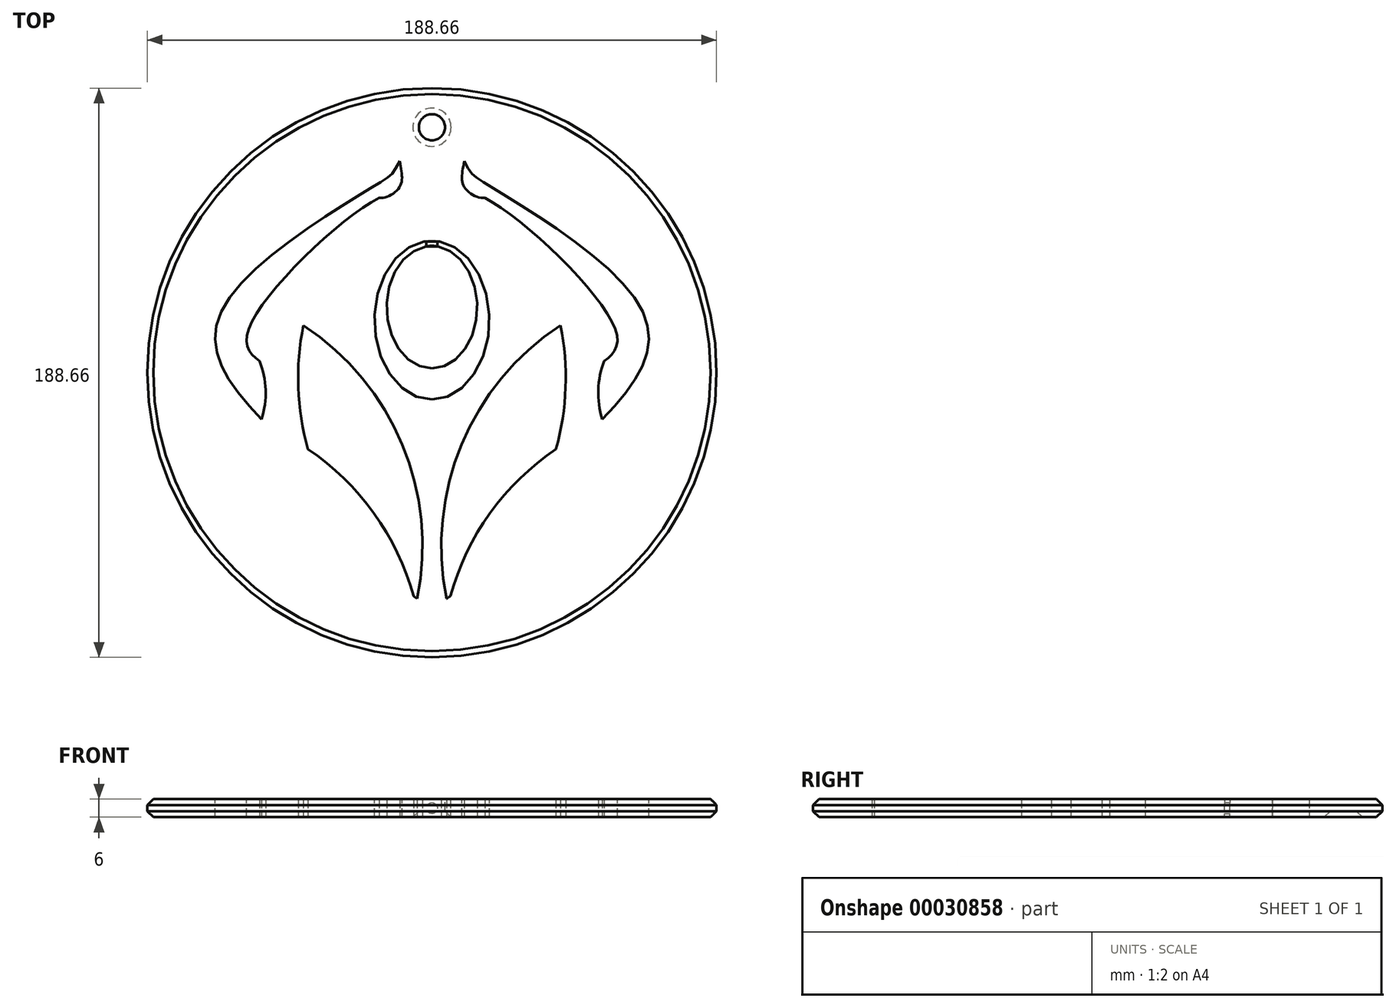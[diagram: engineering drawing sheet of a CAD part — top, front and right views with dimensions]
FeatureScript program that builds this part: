
annotation { "Feature Type Name" : "Feature", "Feature Type Description" : "" }
export const myFeature = defineFeature(function(context is Context, id is Id, definition is map)
    precondition{}
    {
        {
            var Q0;
            Q0=qCreatedBy(makeId("Top.planeOp"),FACE);
            var sketch = newSketch(context, id + "F0", { "sketchPlane" : qUnion([Q0])});
            skLineSegment(sketch, "E0", {"start": v(-75.5, -12.71) * mm, "end": v(-9.56, -74.3) * mm, "construction": true});
            skLineSegment(sketch, "E1", {"start": v(-4.86, -71.61) * mm, "end": v(-42.6, 18.94) * mm, "construction": true});
            skArc(sketch, "E2", {"start": v(-75.5, -12.71) * mm, "mid": v(-51.74, -53.37) * mm, "end": v(-9.56, -74.3) * mm});
            skArc(sketch, "E3", {"start": v(-4.86, -71.61) * mm, "mid": v(-9.83, -20.55) * mm, "end": v(-42.6, 18.94) * mm});
            skArc(sketch, "E4.MirrorCS", {"start": v(-75.5, -12.71) * mm, "mid": v(-33.32, -33.65) * mm, "end": v(-9.56, -74.3) * mm});
            skArc(sketch, "E5.0", {"start": v(-41.12, -22.06) * mm, "mid": v(-19.25, -43.28) * mm, "end": v(-6.12, -70.78) * mm});
            skArc(sketch, "E6.MirrorCS", {"start": v(-4.86, -71.61) * mm, "mid": v(-5.5, -71.2) * mm, "end": v(-6.12, -70.78) * mm});
            skArc(sketch, "E7.trimOffspring", {"start": v(-41.12, -22.06) * mm, "mid": v(-44.3, -1.65) * mm, "end": v(-42.6, 18.94) * mm});
            skArc(sketch, "E8.MirrorCS", {"start": v(75.5, -12.71) * mm, "mid": v(51.74, -53.37) * mm, "end": v(9.56, -74.3) * mm});
            skArc(sketch, "E9.MirrorCS", {"start": v(75.5, -12.71) * mm, "mid": v(33.32, -33.65) * mm, "end": v(9.56, -74.3) * mm});
            skArc(sketch, "E10.MirrorCS", {"start": v(41.12, -22.06) * mm, "mid": v(44.3, -1.65) * mm, "end": v(42.6, 18.94) * mm});
            skArc(sketch, "E11.MirrorCS", {"start": v(41.12, -22.06) * mm, "mid": v(19.25, -43.28) * mm, "end": v(6.12, -70.78) * mm});
            skArc(sketch, "E12.MirrorCS", {"start": v(4.86, -71.61) * mm, "mid": v(9.83, -20.55) * mm, "end": v(42.6, 18.94) * mm});
            skArc(sketch, "E13.MirrorCS", {"start": v(4.86, -71.61) * mm, "mid": v(5.5, -71.2) * mm, "end": v(6.12, -70.78) * mm});
            skSolve(sketch);
        }
        {
            var Q0;
            Q0=qCreatedBy(makeId("Top.planeOp"),FACE);
            var sketch = newSketch(context, id + "F1", { "sketchPlane" : qUnion([Q0])});
            skEllipse(sketch, "E14", {"center": v(0, 20.7) * mm, "majorRadius": 26.3 * mm, "minorRadius": 19.05 * mm, "majorAxis": v(0, -1)});
            skEllipse(sketch, "E15", {"center": v(0, 25) * mm, "majorRadius": 20.32 * mm, "minorRadius": 15 * mm, "majorAxis": v(0, -1)});
            skSolve(sketch);
        }
        {
            var Q0;
            Q0=qCreatedBy(makeId("Top.planeOp"),FACE);
            var sketch = newSketch(context, id + "F2", { "sketchPlane" : qUnion([Q0])});
            skFitSpline(sketch, "E16", {"points": [v(-10.68, 73.41) * mm, v(-17.36, 66.19) * mm, v(-69.53, 24.17) * mm, v(-56.44, -12.12) * mm], "startDerivative": vector(-33.58, -68.78) * mm, "endDerivative": vector(100.3, -102.64) * mm});
            skArc(sketch, "E17", {"start": v(-56.44, -12.12) * mm, "mid": v(-55.12, -2.43) * mm, "end": v(-57.1, 7.15) * mm});
            skFitSpline(sketch, "E18", {"points": [v(-57.1, 7.15) * mm, v(-60.9, 17.24) * mm, v(-17.54, 61.17) * mm], "startDerivative": vector(-32.39, 22.42) * mm, "endDerivative": vector(56.1, 28.88) * mm});
            skFitSpline(sketch, "E19", {"points": [v(-10.68, 73.41) * mm, v(-10.68, 64.87) * mm, v(-17.54, 61.17) * mm], "startDerivative": vector(3.32, -19.88) * mm, "endDerivative": vector(-13.95, 1.21) * mm});
            skFitSpline(sketch, "E20.MirrorCS", {"points": [v(10.68, 73.41) * mm, v(10.68, 64.87) * mm, v(17.54, 61.17) * mm], "startDerivative": vector(-3.32, -19.88) * mm, "endDerivative": vector(13.95, 1.21) * mm});
            skFitSpline(sketch, "E21.MirrorCS", {"points": [v(10.68, 73.41) * mm, v(17.36, 66.19) * mm, v(69.53, 24.17) * mm, v(56.44, -12.12) * mm], "startDerivative": vector(33.58, -68.78) * mm, "endDerivative": vector(-100.3, -102.64) * mm});
            skFitSpline(sketch, "E22.MirrorCS", {"points": [v(57.1, 7.15) * mm, v(60.9, 17.24) * mm, v(17.54, 61.17) * mm], "startDerivative": vector(32.39, 22.42) * mm, "endDerivative": vector(-56.1, 28.88) * mm});
            skArc(sketch, "E23.MirrorCS", {"start": v(56.44, -12.12) * mm, "mid": v(55.12, -2.43) * mm, "end": v(57.1, 7.15) * mm});
            skSolve(sketch);
        }
        {
            var Q0;
            Q0=qCreatedBy(makeId("Top.planeOp"),FACE);
            var sketch = newSketch(context, id + "F3", { "sketchPlane" : qUnion([Q0])});
            skCircle(sketch, "E24", {"center": v(0, 3.28) * mm, "radius": 94.33 * mm});
            skSolve(sketch);
        }
        {
            var Q0;
            Q0=makeQuery(id+"F3.imprint","IMPRINT",FACE,{"disambiguationData":[TD([[makeQuery(id+"F3.imprint","IMPRINT",EDGE,{"derivedFrom":sQuery(id+"F3.wireOp",EDGE,"E24")}),1.0]])]});
            extrude(context, id + "F4", {"entities" : qUnion([Q0]), "endBound" : BoundingType.SYMMETRIC, "depth" : 6 * mm});
        }
        {
            var Q0;
            Q0=makeQuery(id+"F0.imprint","IMPRINT",FACE,{"disambiguationData":[TD([[makeQuery(id+"F0.imprint","IMPRINT",EDGE,{"derivedFrom":sQuery(id+"F0.wireOp",EDGE,"E8.MirrorCS")}),-1.0]])]});
            var Q1;
            Q1=makeQuery(id+"F0.imprint","IMPRINT",FACE,{"disambiguationData":[TD([[makeQuery(id+"F0.imprint","IMPRINT",EDGE,{"derivedFrom":sQuery(id+"F0.wireOp",EDGE,"E10.MirrorCS")}),1.0]])]});
            var Q2;
            Q2=makeQuery(id+"F0.imprint","IMPRINT",FACE,{"disambiguationData":[TD([[makeQuery(id+"F0.imprint","IMPRINT",EDGE,{"derivedFrom":sQuery(id+"F0.wireOp",EDGE,"E3")}),1.0]])]});
            var Q3;
            Q3=makeQuery(id+"F0.imprint","IMPRINT",FACE,{"disambiguationData":[TD([[makeQuery(id+"F0.imprint","IMPRINT",EDGE,{"derivedFrom":sQuery(id+"F0.wireOp",EDGE,"E4.MirrorCS")}),-1.0]])]});
            var Q4;
            Q4=makeQuery(id+"F2.imprint","IMPRINT",FACE,{"disambiguationData":[TD([[makeQuery(id+"F2.imprint","IMPRINT",EDGE,{"derivedFrom":sQuery(id+"F2.wireOp",EDGE,"E16")}),1.0]])]});
            var Q5;
            Q5=makeQuery(id+"F2.imprint","IMPRINT",FACE,{"disambiguationData":[TD([[makeQuery(id+"F2.imprint","IMPRINT",EDGE,{"derivedFrom":sQuery(id+"F2.wireOp",EDGE,"E20.MirrorCS")}),1.0]])]});
            var Q6;
            Q6=makeQuery(id+"F1.imprint","IMPRINT",FACE,{"disambiguationData":[TD([[makeQuery(id+"F1.imprint","IMPRINT",EDGE,{"derivedFrom":sQuery(id+"F1.wireOp",EDGE,"E14")}),1.0]])]});
            extrude(context, id + "F5", {"entities" : qUnion([Q0, Q1, Q2, Q3, Q4, Q5, Q6]), "operationType" : NewBodyOperationType.REMOVE, "endBound" : BoundingType.SYMMETRIC, "depth" : 25 * mm});
        }
        {
            var Q0;
            Q0=qCreatedBy(makeId("Front.planeOp"),FACE);
            cPlane(context, id + "F6", {"entities" : qUnion([Q0]), "cplaneType" : CPlaneType.OFFSET, "offset" : 50 * mm, "oppositeDirection" : true, "width" : 150 * mm, "height" : 150 * mm});
        }
        {
            var Q0;
            Q0=qCreatedBy(id+"F6.planeOp",FACE);
            var sketch = newSketch(context, id + "F7", { "sketchPlane" : qUnion([Q0])});
            skCircle(sketch, "E25", {"center": v(0, 0) * mm, "radius": 1.81 * mm});
            skSolve(sketch);
        }
        {
            var Q0;
            Q0=qSketchRegion(id+"F7",true);
            var Q1;
            Q1=makeQuery(id+"F5.boolean.opBoolean","COPY",FACE,{"derivedFrom":makeQuery(id+"F5.opExtrude","SWEPT_FACE",FACE,{"disambiguationData":[OSD([sQuery(id+"F1.wireOp",EDGE,"E15")])]})});
            extrude(context, id + "F8", {"entities" : qUnion([Q0]), "operationType" : NewBodyOperationType.ADD, "endBound" : BoundingType.UP_TO_SURFACE, "endBoundEntityFace" : qUnion([Q1]), "depth" : 25 * mm});
        }
        {
            var Q0;
            {var subQ0=sQuery(id+"F3.wireOp",EDGE,"E24");Q0=makeQuery(id+"F5.boolean.opBoolean","SPLIT",FACE,{"disambiguationData":[TD([makeQuery(id+"F4.opExtrude","SWEPT_FACE",FACE,{"disambiguationData":[OSD([subQ0])]})])],"derivedFrom":makeQuery(id+"F4.opExtrude","CAP_FACE",FACE,{"disambiguationData":[OSD([subQ0])],"isStart":false})});}
            var sketch = newSketch(context, id + "F9", { "sketchPlane" : qUnion([Q0])});
            skCircle(sketch, "E26", {"center": v(0, 84.63) * mm, "radius": 4.34 * mm});
            skSolve(sketch);
        }
        {
            var Q0;
            Q0=makeQuery(id+"F9.imprint","IMPRINT",FACE,{"disambiguationData":[TD([[makeQuery(id+"F9.imprint","IMPRINT",EDGE,{"derivedFrom":sQuery(id+"F9.wireOp",EDGE,"E26")}),1.0]])]});
            extrude(context, id + "F10", {"entities" : qUnion([Q0]), "operationType" : NewBodyOperationType.REMOVE, "endBound" : BoundingType.THROUGH_ALL, "oppositeDirection" : true, "depth" : 25 * mm});
        }
        {
            var Q0;
            Q0=makeQuery(id+"F4.opExtrude","CAP_EDGE",EDGE,{"disambiguationData":[OSD([sQuery(id+"F3.wireOp",EDGE,"E24")])],"isStart":false});
            var Q1;
            Q1=makeQuery(id+"F4.opExtrude","CAP_EDGE",EDGE,{"disambiguationData":[OSD([sQuery(id+"F3.wireOp",EDGE,"E24")])],"isStart":true});
            var Q2;
            Q2=makeQuery(id+"F10.boolean.opBoolean","COPY",EDGE,{"derivedFrom":makeQuery(id+"F10.opExtrude","CAP_EDGE",EDGE,{"disambiguationData":[OSD([sQuery(id+"F9.wireOp",EDGE,"E26")])],"isStart":true})});
            var Q3;
            {var subQ0=sQuery(id+"F3.wireOp",EDGE,"E24");Q3=makeQuery(id+"F10.boolean.opBoolean","INTERSECT",EDGE,{"derivedFrom":[makeQuery(id+"F5.boolean.opBoolean","SPLIT",FACE,{"disambiguationData":[TD([makeQuery(id+"F4.opExtrude","SWEPT_FACE",FACE,{"disambiguationData":[OSD([subQ0])]})])],"derivedFrom":makeQuery(id+"F4.opExtrude","CAP_FACE",FACE,{"disambiguationData":[OSD([subQ0])],"isStart":true})}),makeQuery(id+"F10.opExtrude","SWEPT_FACE",FACE,{"disambiguationData":[OSD([sQuery(id+"F9.wireOp",EDGE,"E26")])]})]});}
            chamfer(context, id + "F11", {"entities" : qUnion([Q0, Q1, Q2, Q3]), "width" : 2 * mm, "tangentPropagation" : true});
        }
    });
